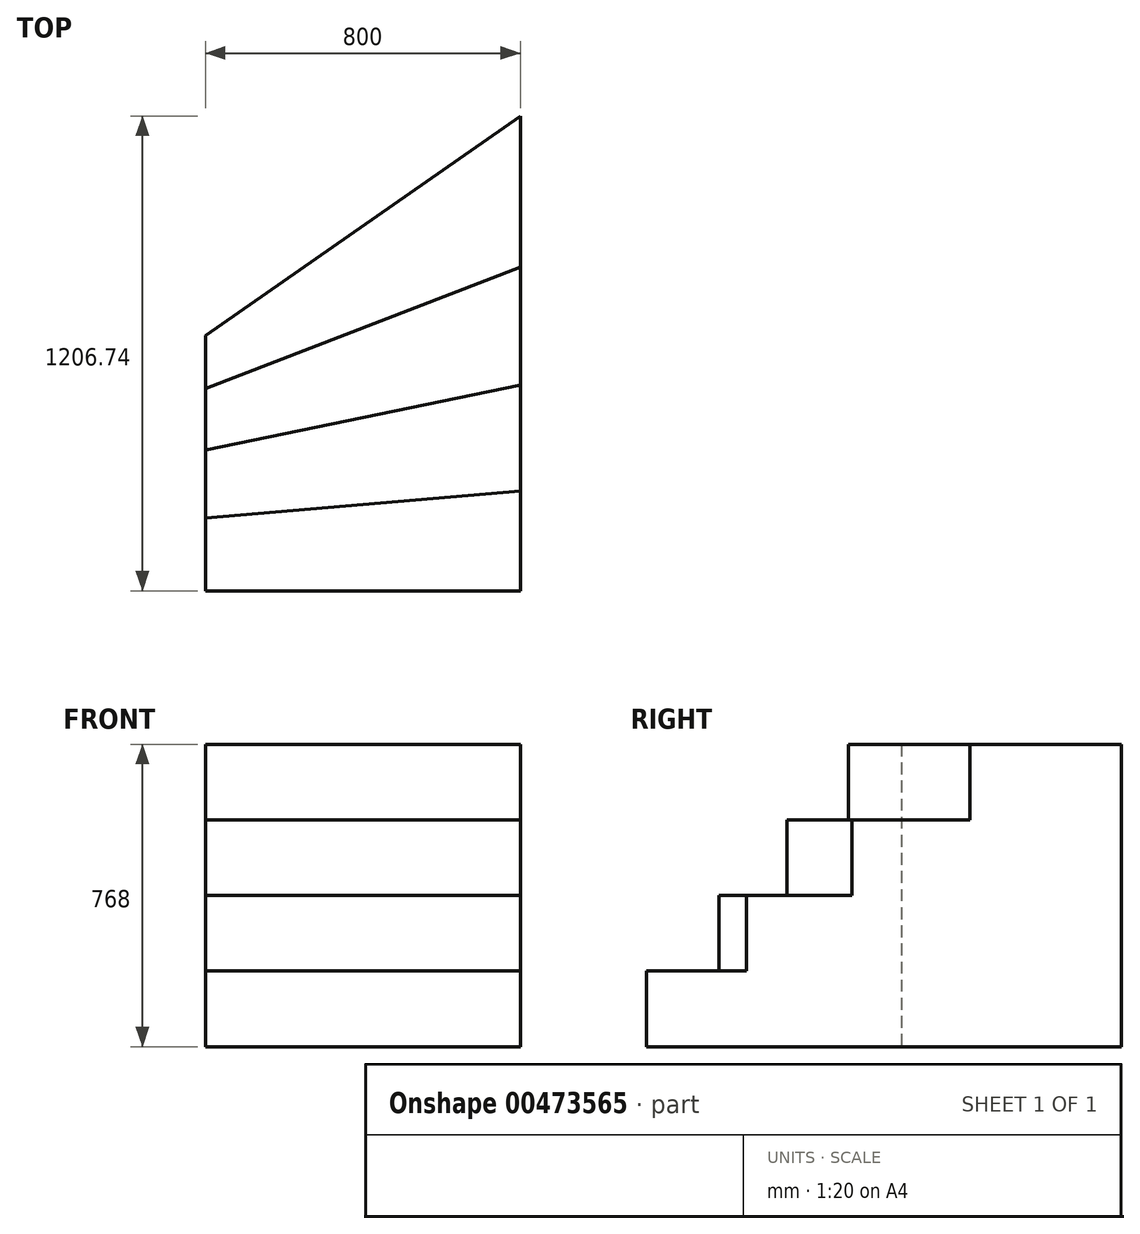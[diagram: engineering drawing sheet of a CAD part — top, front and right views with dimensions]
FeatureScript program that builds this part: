
annotation { "Feature Type Name" : "Feature", "Feature Type Description" : "" }
export const myFeature = defineFeature(function(context is Context, id is Id, definition is map)
    precondition{}
    {
        {
            var Q0;
            Q0=qCreatedBy(makeId("Top.planeOp"),FACE);
            var sketch = newSketch(context, id + "F0", { "sketchPlane" : qUnion([Q0])});
            skLineSegment(sketch, "E0.bottom", {"start": v(-1461.22, 265.68) * mm, "end": v(1188.78, 265.68) * mm});
            skLineSegment(sketch, "E0.left", {"start": v(-1461.22, 265.68) * mm, "end": v(-1461.22, -534.32) * mm});
            skLineSegment(sketch, "E0.right", {"start": v(1188.78, 265.68) * mm, "end": v(1188.78, -1224.32) * mm});
            skLineSegment(sketch, "E1", {"start": v(-1461.22, -534.32) * mm, "end": v(388.78, -534.32) * mm});
            skLineSegment(sketch, "E2", {"start": v(388.78, -534.32) * mm, "end": v(388.78, -1224.32) * mm});
            skLineSegment(sketch, "E3", {"start": v(388.78, -1224.32) * mm, "end": v(1188.78, -1224.32) * mm});
            skLineSegment(sketch, "E4", {"start": v(388.78, -534.32) * mm, "end": v(388.78, 265.68) * mm});
            skLineSegment(sketch, "E5", {"start": v(388.78, -534.32) * mm, "end": v(388.78, -474.32) * mm});
            skLineSegment(sketch, "E6", {"start": v(388.78, -474.32) * mm, "end": v(448.78, -474.32) * mm});
            skLineSegment(sketch, "E7", {"start": v(448.78, -474.32) * mm, "end": v(448.78, -534.32) * mm});
            skLineSegment(sketch, "E8", {"start": v(448.78, -534.32) * mm, "end": v(388.78, -534.32) * mm});
            skLineSegment(sketch, "E9", {"start": v(388.78, -134.32) * mm, "end": v(-1461.22, -134.32) * mm});
            skPoint(sketch, "E10", {"position": v(653.16, -608.6) * mm});
            skPoint(sketch, "E11", {"position": v(158.78, -134.32) * mm});
            skPoint(sketch, "E12", {"position": v(-71.22, -134.32) * mm});
            skPoint(sketch, "E13", {"position": v(-301.22, -134.32) * mm});
            skPoint(sketch, "E14", {"position": v(-531.22, -134.32) * mm});
            skPoint(sketch, "E15", {"position": v(-761.22, -134.32) * mm});
            skPoint(sketch, "E16", {"position": v(-991.22, -134.32) * mm});
            skPoint(sketch, "E17", {"position": v(-1221.22, -134.32) * mm});
            skPoint(sketch, "E18", {"position": v(588.78, -187.91) * mm});
            skPoint(sketch, "E19", {"position": v(735.19, -334.32) * mm});
            skLineSegment(sketch, "E20", {"start": v(588.78, -187.91) * mm, "end": v(388.78, -474.32) * mm});
            skLineSegment(sketch, "E21", {"start": v(735.19, -334.32) * mm, "end": v(448.78, -534.32) * mm});
            skLineSegment(sketch, "E22", {"start": v(588.78, -187.91) * mm, "end": v(986.85, 382.15) * mm});
            skLineSegment(sketch, "E23", {"start": v(388.78, -474.32) * mm, "end": v(-1032.13, -2509.13) * mm});
            skLineSegment(sketch, "E24", {"start": v(735.19, -334.32) * mm, "end": v(1188.78, -17.58) * mm});
            skLineSegment(sketch, "E25", {"start": v(388.78, -1224.32) * mm, "end": v(-1752.51, -1224.32) * mm});
            skPoint(sketch, "E26", {"position": v(-134.95, -1224.32) * mm});
            skPoint(sketch, "E27", {"position": v(-301.22, -1224.32) * mm});
            skPoint(sketch, "E28", {"position": v(-539.34, -1224.32) * mm});
            skLineSegment(sketch, "E29", {"start": v(-301.22, -134.32) * mm, "end": v(-301.22, -1224.32) * mm});
            skLineSegment(sketch, "E30", {"start": v(-301.22, -2176.78) * mm, "end": v(-301.22, -1224.32) * mm});
            skPoint(sketch, "E31", {"position": v(-301.22, -1462.44) * mm});
            skPoint(sketch, "E32", {"position": v(-301.22, -1058.05) * mm});
            skPoint(sketch, "E33", {"position": v(-943.73, -1224.32) * mm});
            skLineSegment(sketch, "E34", {"start": v(-943.73, -1224.32) * mm, "end": v(1188.78, -402.08) * mm});
            skPoint(sketch, "E35", {"position": v(-1348.12, -1224.32) * mm});
            skLineSegment(sketch, "E36", {"start": v(-1348.12, -1224.32) * mm, "end": v(1188.78, -701.4) * mm});
            skLineSegment(sketch, "E37", {"start": v(-1752.51, -1224.32) * mm, "end": v(1188.78, -970.27) * mm});
            skPoint(sketch, "E38", {"position": v(-301.22, -1700.55) * mm});
            skPoint(sketch, "E39", {"position": v(-301.22, -1938.67) * mm});
            skLineSegment(sketch, "E40", {"start": v(-301.22, -1700.55) * mm, "end": v(664.98, 492.64) * mm});
            skLineSegment(sketch, "E41", {"start": v(-301.22, -1938.67) * mm, "end": v(310.06, 459.1) * mm});
            skLineSegment(sketch, "E42", {"start": v(-301.22, -2176.78) * mm, "end": v(0, 498.17) * mm});
            skPoint(sketch, "E43", {"position": v(1188.78, -970.27) * mm});
            skPoint(sketch, "E44", {"position": v(1188.78, -701.4) * mm});
            skPoint(sketch, "E45", {"position": v(1188.78, -402.08) * mm});
            skPoint(sketch, "E46", {"position": v(1188.78, -17.58) * mm});
            skPoint(sketch, "E47", {"position": v(388.78, -1039.37) * mm});
            skPoint(sketch, "E48", {"position": v(388.78, -866.3) * mm});
            skPoint(sketch, "E49", {"position": v(388.78, -710.54) * mm});
            skPoint(sketch, "E50", {"position": v(212.56, -534.32) * mm});
            skPoint(sketch, "E51", {"position": v(56.8, -534.32) * mm});
            skPoint(sketch, "E52", {"position": v(-116.27, -534.32) * mm});
            skPoint(sketch, "E53", {"position": v(905.52, 265.68) * mm});
            skPoint(sketch, "E54", {"position": v(565, 265.68) * mm});
            skPoint(sketch, "E55", {"position": v(260.75, 265.68) * mm});
            skPoint(sketch, "E56", {"position": v(-26.18, 265.68) * mm});
            skPoint(sketch, "E57", {"position": v(448.78, -534.32) * mm});
            skPoint(sketch, "E58", {"position": v(388.78, -576.22) * mm});
            skLineSegment(sketch, "E59", {"start": v(388.78, -576.22) * mm, "end": v(448.78, -534.32) * mm});
            skLineSegment(sketch, "E60", {"start": v(388.78, -576.22) * mm, "end": v(-539.34, -1224.32) * mm});
            skSolve(sketch);
        }
        {
            var Q0;
            {var subQ0=sQuery(id+"F0.wireOp",EDGE,"E3");Q0=makeQuery(id+"F0.imprint","IMPRINT",FACE,{"disambiguationData":[TD([[makeQuery(id+"F0.imprint","IMPRINT",EDGE,{"derivedFrom":subQ0}),1.0]])]});}
            extrude(context, id + "F1", {"entities" : qUnion([Q0]), "depth" : 192 * mm, "offsetDistance" : 25 * mm});
        }
        {
            var Q0;
            {var subQ0=sQuery(id+"F0.wireOp",EDGE,"E36");var subQ1=sQuery(id+"F0.wireOp",EDGE,"E0.right");var subQ2=makeQuery(id+"F0.imprint","INTERSECT",VERTEX,{"derivedFrom":[subQ1,subQ0]});Q0=makeQuery(id+"F0.imprint","IMPRINT",FACE,{"disambiguationData":[TD([[makeQuery(id+"F0.imprint","IMPRINT",EDGE,{"disambiguationData":[TD([[subQ2,-1.0]])],"derivedFrom":subQ1}),-1.0]])]});}
            extrude(context, id + "F2", {"entities" : qUnion([Q0]), "operationType" : NewBodyOperationType.ADD, "depth" : 384 * mm, "offsetDistance" : 25 * mm});
        }
        {
            var Q0;
            {var subQ0=sQuery(id+"F0.wireOp",EDGE,"E34");var subQ1=sQuery(id+"F0.wireOp",EDGE,"E0.right");var subQ2=makeQuery(id+"F0.imprint","INTERSECT",VERTEX,{"derivedFrom":[subQ1,subQ0]});Q0=makeQuery(id+"F0.imprint","IMPRINT",FACE,{"disambiguationData":[TD([[makeQuery(id+"F0.imprint","IMPRINT",EDGE,{"disambiguationData":[TD([[subQ2,-1.0]])],"derivedFrom":subQ1}),-1.0]])]});}
            extrude(context, id + "F3", {"entities" : qUnion([Q0]), "operationType" : NewBodyOperationType.ADD, "depth" : 576 * mm, "offsetDistance" : 25 * mm});
        }
        {
            var Q0;
            {var subQ1=sQuery(id+"F0.wireOp",EDGE,"E21");Q0=makeQuery(id+"F0.imprint","IMPRINT",FACE,{"disambiguationData":[TD([[makeQuery(id+"F0.imprint","IMPRINT",EDGE,{"derivedFrom":subQ1}),1.0]])]});}
            extrude(context, id + "F4", {"entities" : qUnion([Q0]), "operationType" : NewBodyOperationType.ADD, "depth" : 768 * mm, "offsetDistance" : 25 * mm});
        }
    });
